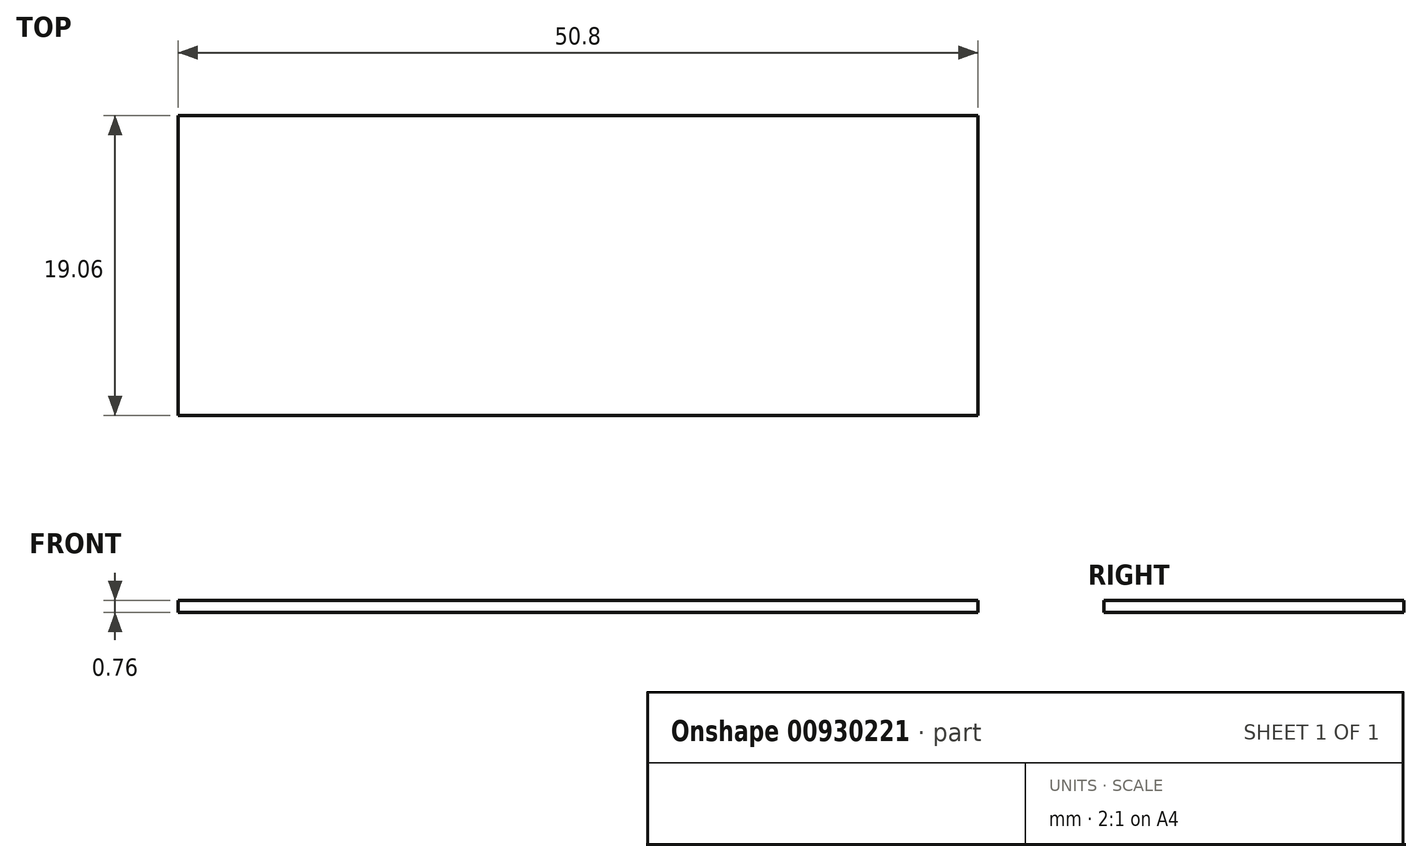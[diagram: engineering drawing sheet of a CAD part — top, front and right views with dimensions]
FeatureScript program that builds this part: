
annotation { "Feature Type Name" : "Feature", "Feature Type Description" : "" }
export const myFeature = defineFeature(function(context is Context, id is Id, definition is map)
    precondition{}
    {
        {
            var Q0;
            Q0=qCreatedBy(makeId("Top.planeOp"),FACE);
            var sketch = newSketch(context, id + "F0", { "sketchPlane" : qUnion([Q0])});
            skLineSegment(sketch, "E0.bottom", {"start": v(25.4, -9.52) * mm, "end": v(-25.4, -9.53) * mm});
            skLineSegment(sketch, "E0.top", {"start": v(25.4, 9.53) * mm, "end": v(-25.4, 9.53) * mm});
            skLineSegment(sketch, "E0.left", {"start": v(25.4, -9.52) * mm, "end": v(25.4, 9.53) * mm});
            skLineSegment(sketch, "E0.right", {"start": v(-25.4, -9.53) * mm, "end": v(-25.4, 9.53) * mm});
            skPoint(sketch, "E0.middle", {"position": v(0, 0) * mm});
            skSolve(sketch);
        }
        {
            var Q0;
            Q0 = qSketchRegion(id + "F0", true);
            extrude(context, id + "F1", {"entities" : qUnion([Q0]), "depth" : 0.76 * mm, "offsetDistance" : 25.4 * mm});
        }
    });
